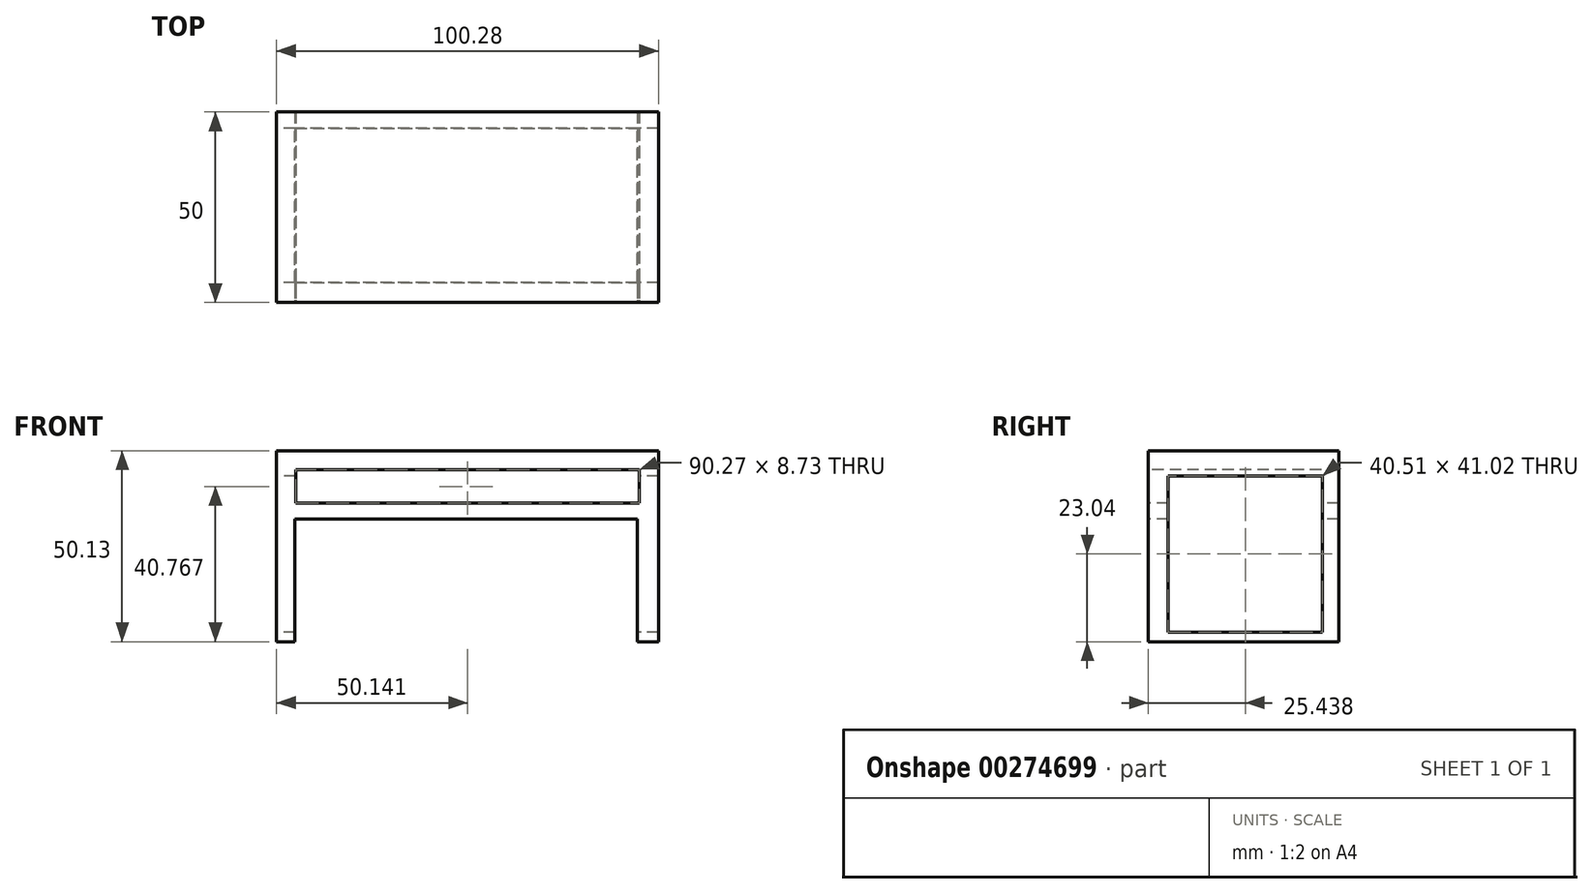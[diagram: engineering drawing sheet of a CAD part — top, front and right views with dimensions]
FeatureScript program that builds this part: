
annotation { "Feature Type Name" : "Feature", "Feature Type Description" : "" }
export const myFeature = defineFeature(function(context is Context, id is Id, definition is map)
    precondition{}
    {
        {
            var Q0;
            Q0=qCreatedBy(makeId("Front.planeOp"),FACE);
            var sketch = newSketch(context, id + "F0", { "sketchPlane" : qUnion([Q0])});
            skLineSegment(sketch, "E0.bottom", {"start": v(-65.84, 56.46) * mm, "end": v(34.44, 56.46) * mm});
            skLineSegment(sketch, "E0.top", {"start": v(-65.84, 6.33) * mm, "end": v(34.44, 6.33) * mm});
            skLineSegment(sketch, "E0.left", {"start": v(-65.84, 56.46) * mm, "end": v(-65.84, 6.33) * mm});
            skLineSegment(sketch, "E0.right", {"start": v(34.44, 56.46) * mm, "end": v(34.44, 6.33) * mm});
            skSolve(sketch);
        }
        {
            var Q0;
            Q0 = qSketchRegion(id + "F0", true);
            extrude(context, id + "F1", {"entities" : qUnion([Q0]), "depth" : 50 * mm});
        }
        {
            var Q0;
            Q0=makeQuery(id+"F1.opExtrude","CAP_FACE",FACE,{"disambiguationData":[OSD([sQuery(id+"F0.wireOp",EDGE,"E0.bottom"),sQuery(id+"F0.wireOp",EDGE,"E0.top"),sQuery(id+"F0.wireOp",EDGE,"E0.left"),sQuery(id+"F0.wireOp",EDGE,"E0.right")])],"isStart":false});
            var sketch = newSketch(context, id + "F2", { "sketchPlane" : qUnion([Q0])});
            skLineSegment(sketch, "E1.bottom", {"start": v(-60.84, 51.46) * mm, "end": v(29.44, 51.46) * mm});
            skLineSegment(sketch, "E1.top", {"start": v(-60.84, 42.73) * mm, "end": v(29.44, 42.73) * mm});
            skLineSegment(sketch, "E1.left", {"start": v(-60.84, 51.46) * mm, "end": v(-60.84, 42.73) * mm});
            skLineSegment(sketch, "E1.right", {"start": v(29.44, 51.46) * mm, "end": v(29.44, 42.73) * mm});
            skSolve(sketch);
        }
        {
            var Q0;
            Q0=makeQuery(id+"F2.imprint","IMPRINT",FACE,{"disambiguationData":[TD([[makeQuery(id+"F2.imprint","IMPRINT",EDGE,{"derivedFrom":sQuery(id+"F2.wireOp",EDGE,"E1.bottom")}),-1.0]])]});
            extrude(context, id + "F3", {"entities" : qUnion([Q0]), "operationType" : NewBodyOperationType.REMOVE, "endBound" : BoundingType.THROUGH_ALL, "oppositeDirection" : true, "depth" : 25 * mm});
        }
        {
            var Q0;
            Q0=makeQuery(id+"F1.opExtrude","SWEPT_FACE",FACE,{"disambiguationData":[OSD([sQuery(id+"F0.wireOp",EDGE,"E0.left")])]});
            var sketch = newSketch(context, id + "F4", { "sketchPlane" : qUnion([Q0])});
            skSolve(sketch);
        }
        {
            var Q0;
            {var subQ0=sQuery(id+"F0.wireOp",EDGE,"E0.left");Q0=makeQuery(id+"F4.imprint","IMPRINT",FACE,{"disambiguationData":[TD([[makeQuery(id+"F4.imprint","IMPRINT",EDGE,{"derivedFrom":makeQuery(id+"F1.opExtrude","CAP_EDGE",EDGE,{"disambiguationData":[OSD([subQ0])],"isStart":true})}),1.0]])]});}
            var sketch = newSketch(context, id + "F5", { "sketchPlane" : qUnion([Q0])});
            skLineSegment(sketch, "E2.bottom", {"start": v(4.3, 49.88) * mm, "end": v(44.82, 49.88) * mm});
            skLineSegment(sketch, "E2.top", {"start": v(4.3, 8.86) * mm, "end": v(44.82, 8.86) * mm});
            skLineSegment(sketch, "E2.left", {"start": v(4.3, 49.88) * mm, "end": v(4.3, 8.86) * mm});
            skLineSegment(sketch, "E2.right", {"start": v(44.82, 49.88) * mm, "end": v(44.82, 8.86) * mm});
            skSolve(sketch);
        }
        {
            var Q0;
            Q0 = qSketchRegion(id + "F5", true);
            extrude(context, id + "F6", {"entities" : qUnion([Q0]), "operationType" : NewBodyOperationType.REMOVE, "endBound" : BoundingType.THROUGH_ALL, "oppositeDirection" : true, "depth" : 25 * mm});
        }
        {
            var Q0;
            Q0=makeQuery(id+"F1.opExtrude","CAP_FACE",FACE,{"disambiguationData":[OSD([sQuery(id+"F0.wireOp",EDGE,"E0.bottom"),sQuery(id+"F0.wireOp",EDGE,"E0.top"),sQuery(id+"F0.wireOp",EDGE,"E0.left"),sQuery(id+"F0.wireOp",EDGE,"E0.right")])],"isStart":false});
            var sketch = newSketch(context, id + "F7", { "sketchPlane" : qUnion([Q0])});
            skLineSegment(sketch, "E3.bottom", {"start": v(-61.02, 38.49) * mm, "end": v(28.87, 38.49) * mm});
            skLineSegment(sketch, "E3.top", {"start": v(-61.02, 6.33) * mm, "end": v(28.87, 6.33) * mm});
            skLineSegment(sketch, "E3.left", {"start": v(-61.02, 38.49) * mm, "end": v(-61.02, 6.33) * mm});
            skLineSegment(sketch, "E3.right", {"start": v(28.87, 38.49) * mm, "end": v(28.87, 6.33) * mm});
            skSolve(sketch);
        }
        {
            var Q0;
            Q0 = qSketchRegion(id + "F7", true);
            extrude(context, id + "F8", {"entities" : qUnion([Q0]), "operationType" : NewBodyOperationType.REMOVE, "endBound" : BoundingType.THROUGH_ALL, "oppositeDirection" : true, "depth" : 25 * mm});
        }
    });
